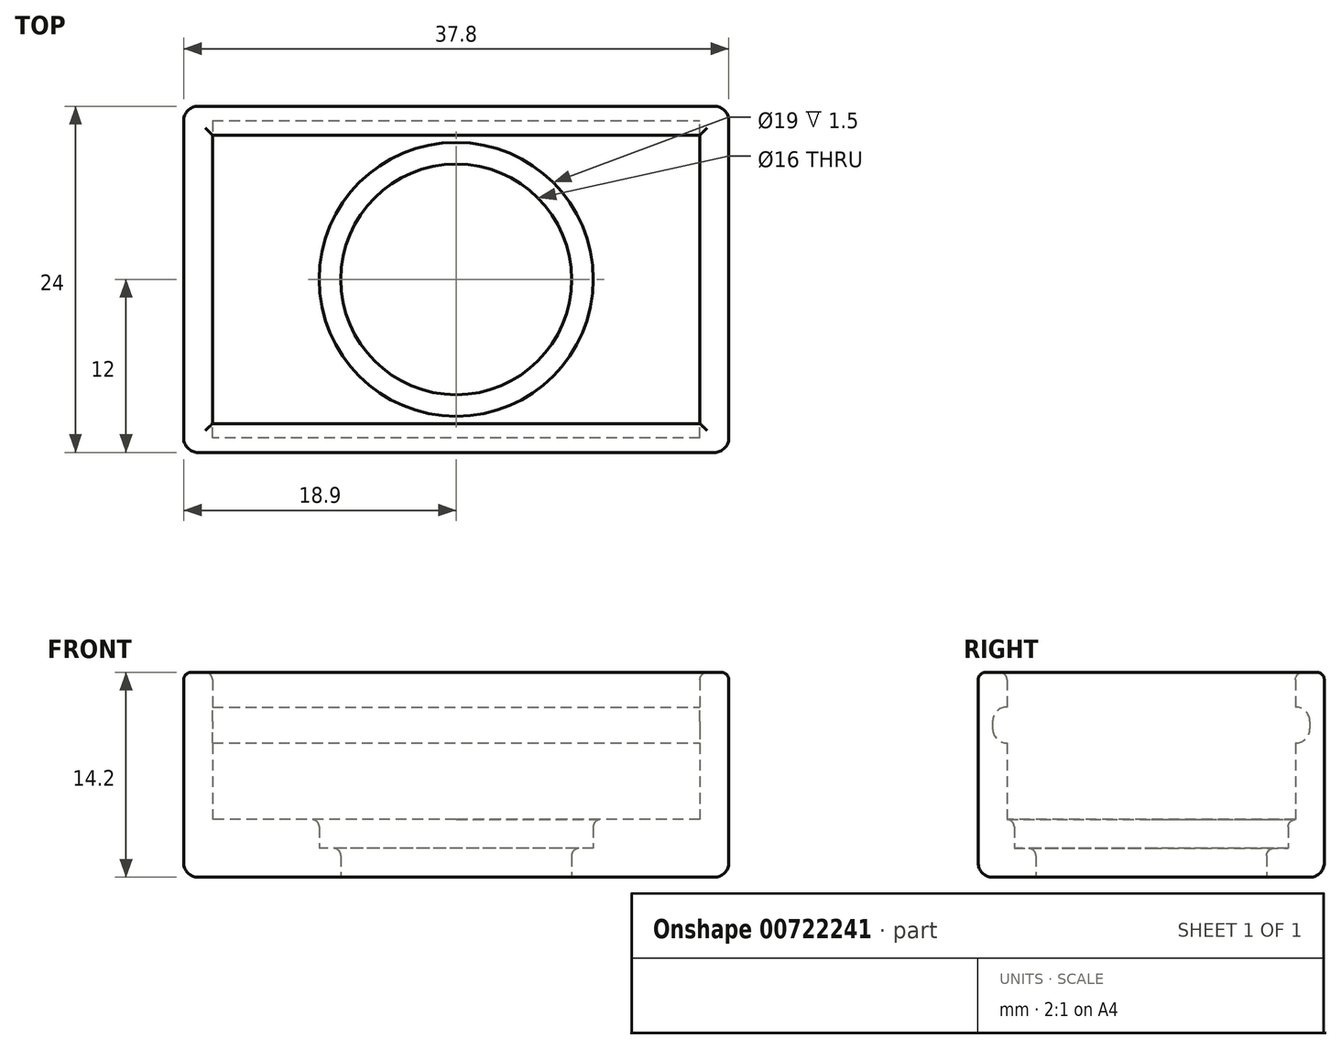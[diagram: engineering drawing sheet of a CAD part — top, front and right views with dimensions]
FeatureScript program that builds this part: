
annotation { "Feature Type Name" : "Feature", "Feature Type Description" : "" }
export const myFeature = defineFeature(function(context is Context, id is Id, definition is map)
    precondition{}
    {
        {
            var Q0;
            Q0=qCreatedBy(makeId("Top.planeOp"),FACE);
            var sketch = newSketch(context, id + "F0", { "sketchPlane" : qUnion([Q0])});
            skLineSegment(sketch, "E0.bottom", {"start": v(16.9, -10) * mm, "end": v(-16.9, -10) * mm});
            skLineSegment(sketch, "E0.top", {"start": v(16.9, 10) * mm, "end": v(-16.9, 10) * mm});
            skLineSegment(sketch, "E0.left", {"start": v(16.9, -10) * mm, "end": v(16.9, 10) * mm});
            skLineSegment(sketch, "E0.right", {"start": v(-16.9, -10) * mm, "end": v(-16.9, 10) * mm});
            skPoint(sketch, "E0.middle", {"position": v(0, 0) * mm});
            skLineSegment(sketch, "E1.bottom", {"start": v(18.9, -12) * mm, "end": v(-18.9, -12) * mm});
            skLineSegment(sketch, "E1.top", {"start": v(18.9, 12) * mm, "end": v(-18.9, 12) * mm});
            skLineSegment(sketch, "E1.left", {"start": v(18.9, -12) * mm, "end": v(18.9, 12) * mm});
            skLineSegment(sketch, "E1.right", {"start": v(-18.9, -12) * mm, "end": v(-18.9, 12) * mm});
            skCircle(sketch, "E2", {"center": v(0, 0) * mm, "radius": 8 * mm});
            skCircle(sketch, "E3", {"center": v(0, 0) * mm, "radius": 9.5 * mm});
            skSolve(sketch);
        }
        {
            var Q0;
            Q0=makeQuery(id+"F0.imprint","IMPRINT",FACE,{"disambiguationData":[TD([[makeQuery(id+"F0.imprint","IMPRINT",EDGE,{"derivedFrom":sQuery(id+"F0.wireOp",EDGE,"E0.bottom")}),1.0]])]});
            extrude(context, id + "F1", {"entities" : qUnion([Q0]), "depth" : 14.2 * mm, "offsetDistance" : 25 * mm});
        }
        {
            var Q0;
            Q0=makeQuery(id+"F0.imprint","IMPRINT",FACE,{"disambiguationData":[TD([[makeQuery(id+"F0.imprint","IMPRINT",EDGE,{"derivedFrom":sQuery(id+"F0.wireOp",EDGE,"E0.bottom")}),-1.0]])]});
            extrude(context, id + "F2", {"entities" : qUnion([Q0]), "operationType" : NewBodyOperationType.ADD, "depth" : 4 * mm, "offsetDistance" : 25 * mm});
        }
        {
            var Q0;
            Q0=makeQuery(id+"F0.imprint","IMPRINT",FACE,{"disambiguationData":[TD([[makeQuery(id+"F0.imprint","IMPRINT",EDGE,{"derivedFrom":sQuery(id+"F0.wireOp",EDGE,"E2")}),-1.0]])]});
            extrude(context, id + "F3", {"entities" : qUnion([Q0]), "operationType" : NewBodyOperationType.ADD, "depth" : 2 * mm, "offsetDistance" : 25 * mm});
        }
        {
            var Q0;
            Q0=makeQuery(id+"F1.opExtrude","SWEPT_FACE",FACE,{"disambiguationData":[OSD([sQuery(id+"F0.wireOp",EDGE,"E0.top")])]});
            var sketch = newSketch(context, id + "F4", { "sketchPlane" : qUnion([Q0])});
            skLineSegment(sketch, "E4", {"start": v(0, 4) * mm, "end": v(0, 9.3) * mm, "construction": true});
            skLineSegment(sketch, "E5", {"start": v(0, 9.3) * mm, "end": v(-16.9, 9.3) * mm, "construction": true});
            skLineSegment(sketch, "E6", {"start": v(-16.9, 9.3) * mm, "end": v(16.9, 9.3) * mm});
            skLineSegment(sketch, "E7", {"start": v(-16.9, 11.8) * mm, "end": v(16.9, 11.8) * mm});
            skSolve(sketch);
        }
        {
            var Q0;
            {var subQ0=sQuery(id+"F4.wireOp",EDGE,"E6");Q0=makeQuery(id+"F4.imprint","IMPRINT",FACE,{"disambiguationData":[TD([[makeQuery(id+"F4.imprint","IMPRINT",EDGE,{"derivedFrom":subQ0}),1.0]])]});}
            extrude(context, id + "F5", {"entities" : qUnion([Q0]), "operationType" : NewBodyOperationType.REMOVE, "oppositeDirection" : true, "depth" : 1 * mm, "offsetDistance" : 25 * mm});
        }
        {
            var Q0;
            Q0=makeQuery(id+"F1.opExtrude","SWEPT_FACE",FACE,{"disambiguationData":[OSD([sQuery(id+"F0.wireOp",EDGE,"E0.bottom")])]});
            var sketch = newSketch(context, id + "F6", { "sketchPlane" : qUnion([Q0])});
            skLineSegment(sketch, "E8", {"start": v(1.56, 4) * mm, "end": v(1.56, 9.3) * mm});
            skLineSegment(sketch, "E9", {"start": v(1.56, 9.3) * mm, "end": v(-16.9, 9.3) * mm});
            skPoint(sketch, "E9.endSnap0", {"position": v(-16.9, 9.1) * mm});
            skLineSegment(sketch, "E10", {"start": v(1.56, 9.3) * mm, "end": v(16.9, 9.3) * mm});
            skLineSegment(sketch, "E11", {"start": v(-16.9, 11.8) * mm, "end": v(16.9, 11.8) * mm});
            skSolve(sketch);
        }
        {
            var Q0;
            {var subQ1=sQuery(id+"F6.wireOp",EDGE,"E9");Q0=makeQuery(id+"F6.imprint","IMPRINT",FACE,{"disambiguationData":[TD([[makeQuery(id+"F6.imprint","IMPRINT",EDGE,{"derivedFrom":subQ1}),-1.0]])]});}
            extrude(context, id + "F7", {"entities" : qUnion([Q0]), "operationType" : NewBodyOperationType.REMOVE, "oppositeDirection" : true, "depth" : 1 * mm, "offsetDistance" : 25 * mm});
        }
        {
            var Q0;
            Q0=makeQuery(id+"F2.opExtrude","CAP_EDGE",EDGE,{"disambiguationData":[OSD([sQuery(id+"F0.wireOp",EDGE,"E3")])],"isStart":false});
            var Q1;
            Q1=makeQuery(id+"F3.opExtrude","CAP_EDGE",EDGE,{"disambiguationData":[OSD([sQuery(id+"F0.wireOp",EDGE,"E2")])],"isStart":false});
            var Q2;
            Q2=makeQuery(id+"F1.opExtrude","CAP_EDGE",EDGE,{"disambiguationData":[OSD([sQuery(id+"F0.wireOp",EDGE,"E0.top")])],"isStart":false});
            var Q3;
            Q3=makeQuery(id+"F1.opExtrude","CAP_EDGE",EDGE,{"disambiguationData":[OSD([sQuery(id+"F0.wireOp",EDGE,"E0.left")])],"isStart":false});
            var Q4;
            Q4=makeQuery(id+"F1.opExtrude","CAP_EDGE",EDGE,{"disambiguationData":[OSD([sQuery(id+"F0.wireOp",EDGE,"E0.right")])],"isStart":false});
            var Q5;
            Q5=makeQuery(id+"F1.opExtrude","CAP_EDGE",EDGE,{"disambiguationData":[OSD([sQuery(id+"F0.wireOp",EDGE,"E0.bottom")])],"isStart":false});
            var Q6;
            Q6=makeQuery(id+"F1.opExtrude","CAP_FACE",FACE,{"disambiguationData":[OSD([sQuery(id+"F0.wireOp",EDGE,"E0.bottom"),sQuery(id+"F0.wireOp",EDGE,"E0.top"),sQuery(id+"F0.wireOp",EDGE,"E0.left"),sQuery(id+"F0.wireOp",EDGE,"E0.right"),sQuery(id+"F0.wireOp",EDGE,"E1.bottom"),sQuery(id+"F0.wireOp",EDGE,"E1.top"),sQuery(id+"F0.wireOp",EDGE,"E1.left"),sQuery(id+"F0.wireOp",EDGE,"E1.right")])],"isStart":false});
            fillet(context, id + "F8", {"entities" : qUnion([Q0, Q1, Q2, Q3, Q4, Q5, Q6]), "radius" : .5 * mm, "tangentPropagation" : true, "allowEdgeOverflow" : false});
        }
        {
            var Q0;
            Q0=makeQuery(id+"F5.boolean.opBoolean","COPY",EDGE,{"derivedFrom":makeQuery(id+"F5.opExtrude","CAP_EDGE",EDGE,{"disambiguationData":[OSD([sQuery(id+"F4.wireOp",EDGE,"E6")])],"isStart":false})});
            var Q1;
            Q1=makeQuery(id+"F5.boolean.opBoolean","COPY",EDGE,{"derivedFrom":makeQuery(id+"F5.opExtrude","CAP_EDGE",EDGE,{"disambiguationData":[OSD([sQuery(id+"F4.wireOp",EDGE,"E7")])],"isStart":false})});
            var Q2;
            Q2=makeQuery(id+"F7.boolean.opBoolean","COPY",EDGE,{"derivedFrom":makeQuery(id+"F7.opExtrude","CAP_EDGE",EDGE,{"disambiguationData":[OSD([sQuery(id+"F6.wireOp",EDGE,"E9"),sQuery(id+"F6.wireOp",EDGE,"E10")])],"isStart":false})});
            var Q3;
            Q3=makeQuery(id+"F7.boolean.opBoolean","COPY",EDGE,{"derivedFrom":makeQuery(id+"F7.opExtrude","CAP_EDGE",EDGE,{"disambiguationData":[OSD([sQuery(id+"F6.wireOp",EDGE,"E11")])],"isStart":false})});
            fillet(context, id + "F9", {"entities" : qUnion([Q0, Q1, Q2, Q3]), "radius" : 1 * mm, "tangentPropagation" : true, "allowEdgeOverflow" : false});
        }
        {
            var Q0;
            Q0=makeQuery(id+"F1.opExtrude","CAP_EDGE",EDGE,{"disambiguationData":[OSD([sQuery(id+"F0.wireOp",EDGE,"E1.bottom")])],"isStart":true});
            var Q1;
            Q1=makeQuery(id+"F1.opExtrude","CAP_EDGE",EDGE,{"disambiguationData":[OSD([sQuery(id+"F0.wireOp",EDGE,"E1.right")])],"isStart":true});
            var Q2;
            Q2=makeQuery(id+"F1.opExtrude","CAP_EDGE",EDGE,{"disambiguationData":[OSD([sQuery(id+"F0.wireOp",EDGE,"E1.top")])],"isStart":true});
            var Q3;
            Q3=makeQuery(id+"F1.opExtrude","CAP_EDGE",EDGE,{"disambiguationData":[OSD([sQuery(id+"F0.wireOp",EDGE,"E1.left")])],"isStart":true});
            var Q4;
            Q4=makeQuery(id+"F1.opExtrude","SWEPT_EDGE",EDGE,{"disambiguationData":[OSD([sQuery(id+"F0.wireOp",EDGE,"E1.bottom"),sQuery(id+"F0.wireOp",EDGE,"E1.left")])]});
            var Q5;
            Q5=makeQuery(id+"F1.opExtrude","SWEPT_EDGE",EDGE,{"disambiguationData":[OSD([sQuery(id+"F0.wireOp",EDGE,"E1.bottom"),sQuery(id+"F0.wireOp",EDGE,"E1.right")])]});
            var Q6;
            Q6=makeQuery(id+"F1.opExtrude","SWEPT_EDGE",EDGE,{"disambiguationData":[OSD([sQuery(id+"F0.wireOp",EDGE,"E1.top"),sQuery(id+"F0.wireOp",EDGE,"E1.left")])]});
            var Q7;
            Q7=makeQuery(id+"F1.opExtrude","SWEPT_EDGE",EDGE,{"disambiguationData":[OSD([sQuery(id+"F0.wireOp",EDGE,"E1.top"),sQuery(id+"F0.wireOp",EDGE,"E1.right")])]});
            fillet(context, id + "F10", {"entities" : qUnion([Q0, Q1, Q2, Q3, Q4, Q5, Q6, Q7]), "radius" : 1 * mm, "tangentPropagation" : true, "allowEdgeOverflow" : false});
        }
    });
